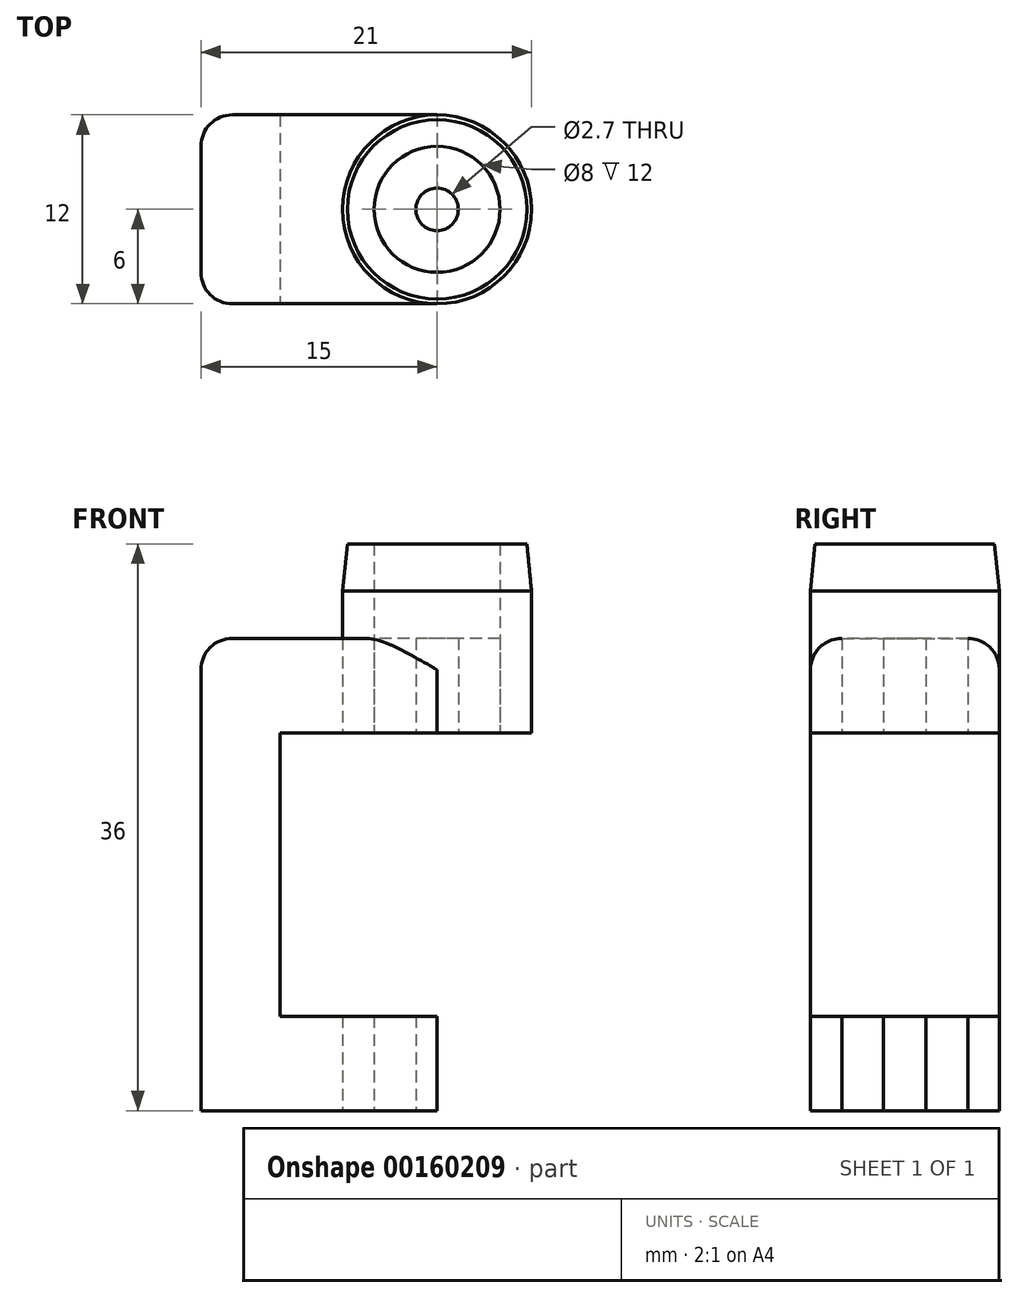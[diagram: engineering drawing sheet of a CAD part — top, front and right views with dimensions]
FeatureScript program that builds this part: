
annotation { "Feature Type Name" : "Feature", "Feature Type Description" : "" }
export const myFeature = defineFeature(function(context is Context, id is Id, definition is map)
    precondition{}
    {
        {
            var Q0;
            Q0=qCreatedBy(makeId("Top.planeOp"),FACE);
            var sketch = newSketch(context, id + "F3", { "sketchPlane" : qUnion([Q0])});
            skCircle(sketch, "E0", {"center": v(0, 0) * mm, "radius": 6 * mm});
            skCircle(sketch, "E1", {"center": v(0, 0) * mm, "radius": 1.35 * mm});
            skCircle(sketch, "E2", {"center": v(0, 0) * mm, "radius": 4 * mm});
            skLineSegment(sketch, "E3.bottom", {"start": v(0, 6) * mm, "end": v(-13, 6) * mm});
            skLineSegment(sketch, "E3.top", {"start": v(0, -6) * mm, "end": v(-13, -6) * mm});
            skLineSegment(sketch, "E3.left", {"start": v(0, 6) * mm, "end": v(0, -6) * mm});
            skLineSegment(sketch, "E3.right", {"start": v(-15, 4) * mm, "end": v(-15, -4) * mm});
            skPoint(sketch, "E4.visualSharp", {"position": v(-15, -6) * mm});
            skArc(sketch, "E4.filletArc", {"start": v(-15, -4) * mm, "mid": v(-14.41, -5.41) * mm, "end": v(-13, -6) * mm});
            skPoint(sketch, "E5.visualSharp", {"position": v(-15, 6) * mm});
            skArc(sketch, "E5.filletArc", {"start": v(-13, 6) * mm, "mid": v(-14.41, 5.41) * mm, "end": v(-15, 4) * mm});
            skSolve(sketch);
        }
        {
            var Q0;
            {var subQ0=sQuery(id+"F3.wireOp",EDGE,"E3.left");var subQ1=sQuery(id+"F3.wireOp",EDGE,"E1");var subQ2=makeQuery(id+"F3.imprint","INTERSECT",VERTEX,{"disambiguationData":[OD(0.0)],"derivedFrom":[subQ1,subQ0]});Q0=makeQuery(id+"F3.imprint","IMPRINT",FACE,{"disambiguationData":[TD([[makeQuery(id+"F3.imprint","IMPRINT",EDGE,{"disambiguationData":[TD([[subQ2,-1.0]])],"derivedFrom":subQ1}),-1.0]])]});}
            var Q1;
            {var subQ0=sQuery(id+"F3.wireOp",EDGE,"E3.left");var subQ1=sQuery(id+"F3.wireOp",EDGE,"E1");var subQ2=makeQuery(id+"F3.imprint","INTERSECT",VERTEX,{"disambiguationData":[OD(0.0)],"derivedFrom":[subQ1,subQ0]});Q1=makeQuery(id+"F3.imprint","IMPRINT",FACE,{"disambiguationData":[TD([[makeQuery(id+"F3.imprint","IMPRINT",EDGE,{"disambiguationData":[TD([[subQ2,1.0]])],"derivedFrom":subQ1}),-1.0]])]});}
            var Q2;
            {var subQ0=sQuery(id+"F3.wireOp",EDGE,"E3.bottom");Q2=makeQuery(id+"F3.imprint","IMPRINT",FACE,{"disambiguationData":[TD([[makeQuery(id+"F3.imprint","IMPRINT",EDGE,{"derivedFrom":subQ0}),1.0]])]});}
            extrude(context, id + "F4", {"entities" : qUnion([Q0, Q1, Q2]), "depth" : 30 * mm});
        }
        {
            var Q0;
            {var subQ0=sQuery(id+"F3.wireOp",EDGE,"E3.left");var subQ4=sQuery(id+"F3.wireOp",EDGE,"E2");var subQ5=makeQuery(id+"F3.imprint","INTERSECT",VERTEX,{"disambiguationData":[OD(0.0)],"derivedFrom":[subQ4,subQ0]});Q0=makeQuery(id+"F3.imprint","IMPRINT",FACE,{"disambiguationData":[TD([[makeQuery(id+"F3.imprint","IMPRINT",EDGE,{"disambiguationData":[TD([[subQ5,-1.0]])],"derivedFrom":subQ4}),-1.0]])]});}
            var Q1;
            {var subQ0=sQuery(id+"F3.wireOp",EDGE,"E3.left");var subQ4=sQuery(id+"F3.wireOp",EDGE,"E2");var subQ5=makeQuery(id+"F3.imprint","INTERSECT",VERTEX,{"disambiguationData":[OD(0.0)],"derivedFrom":[subQ4,subQ0]});Q1=makeQuery(id+"F3.imprint","IMPRINT",FACE,{"disambiguationData":[TD([[makeQuery(id+"F3.imprint","IMPRINT",EDGE,{"disambiguationData":[TD([[subQ5,1.0]])],"derivedFrom":subQ4}),-1.0]])]});}
            extrude(context, id + "F5", {"entities" : qUnion([Q0, Q1]), "depth" : 36 * mm});
        }
        {
            var Q0;
            Q0=makeQuery(id+"F5.opExtrude","CAP_EDGE",EDGE,{"disambiguationData":[OSD([sQuery(id+"F3.wireOp",EDGE,"E0")])],"isStart":false});
            chamfer(context, id + "F0", {"entities" : qUnion([Q0]), "chamferType" : ChamferType.TWO_OFFSETS, "width1" : 3 * mm, "oppositeDirection" : true, "width2" : 0.3 * mm, "tangentPropagation" : true});
        }
        {
            var Q0;
            Q0=makeQuery(id+"F4.opExtrude","SWEPT_FACE",FACE,{"disambiguationData":[OSD([sQuery(id+"F3.wireOp",EDGE,"E3.top")])]});
            var sketch = newSketch(context, id + "F6", { "sketchPlane" : qUnion([Q0])});
            skLineSegment(sketch, "E6.bottom", {"start": v(6, 24) * mm, "end": v(-9.99, 24) * mm});
            skLineSegment(sketch, "E6.top", {"start": v(6, 6) * mm, "end": v(-9.99, 6) * mm});
            skLineSegment(sketch, "E6.left", {"start": v(6, 24) * mm, "end": v(6, 6) * mm});
            skLineSegment(sketch, "E6.right", {"start": v(-9.99, 24) * mm, "end": v(-9.99, 6) * mm});
            skLineSegment(sketch, "E7.0", {"start": v(0, 30) * mm, "end": v(-13, 30) * mm});
            skLineSegment(sketch, "E8.0", {"start": v(-13, 30) * mm, "end": v(-13, 0) * mm});
            skLineSegment(sketch, "E9.0", {"start": v(0, 0) * mm, "end": v(-13, 0) * mm});
            skLineSegment(sketch, "E10.0", {"start": v(-6, 0) * mm, "end": v(6, 0) * mm});
            skLineSegment(sketch, "E11", {"start": v(6, 33) * mm, "end": v(6, 0) * mm});
            skSolve(sketch);
        }
        {
            var Q0;
            {var subQ0=sQuery(id+"F6.wireOp",EDGE,"E6.right");Q0=makeQuery(id+"F6.imprint","IMPRINT",FACE,{"disambiguationData":[TD([[makeQuery(id+"F6.imprint","IMPRINT",EDGE,{"derivedFrom":subQ0}),1.0]])]});}
            var Q1;
            {var subQ0=sQuery(id+"F6.wireOp",EDGE,"E6.left");Q1=makeQuery(id+"F6.imprint","IMPRINT",FACE,{"disambiguationData":[TD([[makeQuery(id+"F6.imprint","IMPRINT",EDGE,{"derivedFrom":subQ0}),-1.0]])]});}
            var Q2;
            {var subQ0=sQuery(id+"F6.wireOp",EDGE,"E11");var subQ1=sQuery(id+"F6.wireOp",EDGE,"E6.bottom");var subQ2=makeQuery(id+"F6.imprint","INTERSECT",VERTEX,{"derivedFrom":[subQ1,subQ0]});Q2=makeQuery(id+"F6.imprint","IMPRINT",FACE,{"disambiguationData":[TD([[makeQuery(id+"F6.imprint","IMPRINT",EDGE,{"disambiguationData":[TD([[subQ2,-1.0]])],"derivedFrom":subQ0}),-1.0]])]});}
            extrude(context, id + "F7", {"entities" : qUnion([Q0, Q1, Q2]), "operationType" : NewBodyOperationType.REMOVE, "oppositeDirection" : true, "depth" : 25 * mm});
        }
        {
            var Q0;
            {var subQ0=sQuery(id+"F6.wireOp",EDGE,"E6.right");Q0=makeQuery(id+"F6.imprint","IMPRINT",FACE,{"disambiguationData":[TD([[makeQuery(id+"F6.imprint","IMPRINT",EDGE,{"derivedFrom":subQ0}),1.0]])]});}
            var Q1;
            {var subQ0=sQuery(id+"F6.wireOp",EDGE,"E6.left");Q1=makeQuery(id+"F6.imprint","IMPRINT",FACE,{"disambiguationData":[TD([[makeQuery(id+"F6.imprint","IMPRINT",EDGE,{"derivedFrom":subQ0}),-1.0]])]});}
            extrude(context, id + "F1", {"entities" : qUnion([Q0, Q1]), "operationType" : NewBodyOperationType.REMOVE, "depth" : 25 * mm});
        }
        {
            var Q0;
            Q0=makeQuery(id+"F4.opExtrude","CAP_EDGE",EDGE,{"disambiguationData":[OSD([sQuery(id+"F3.wireOp",EDGE,"E3.right")])],"isStart":false});
            fillet(context, id + "F2", {"entities" : qUnion([Q0]), "radius" : 2 * mm, "tangentPropagation" : true, "allowEdgeOverflow" : false});
        }
    });
